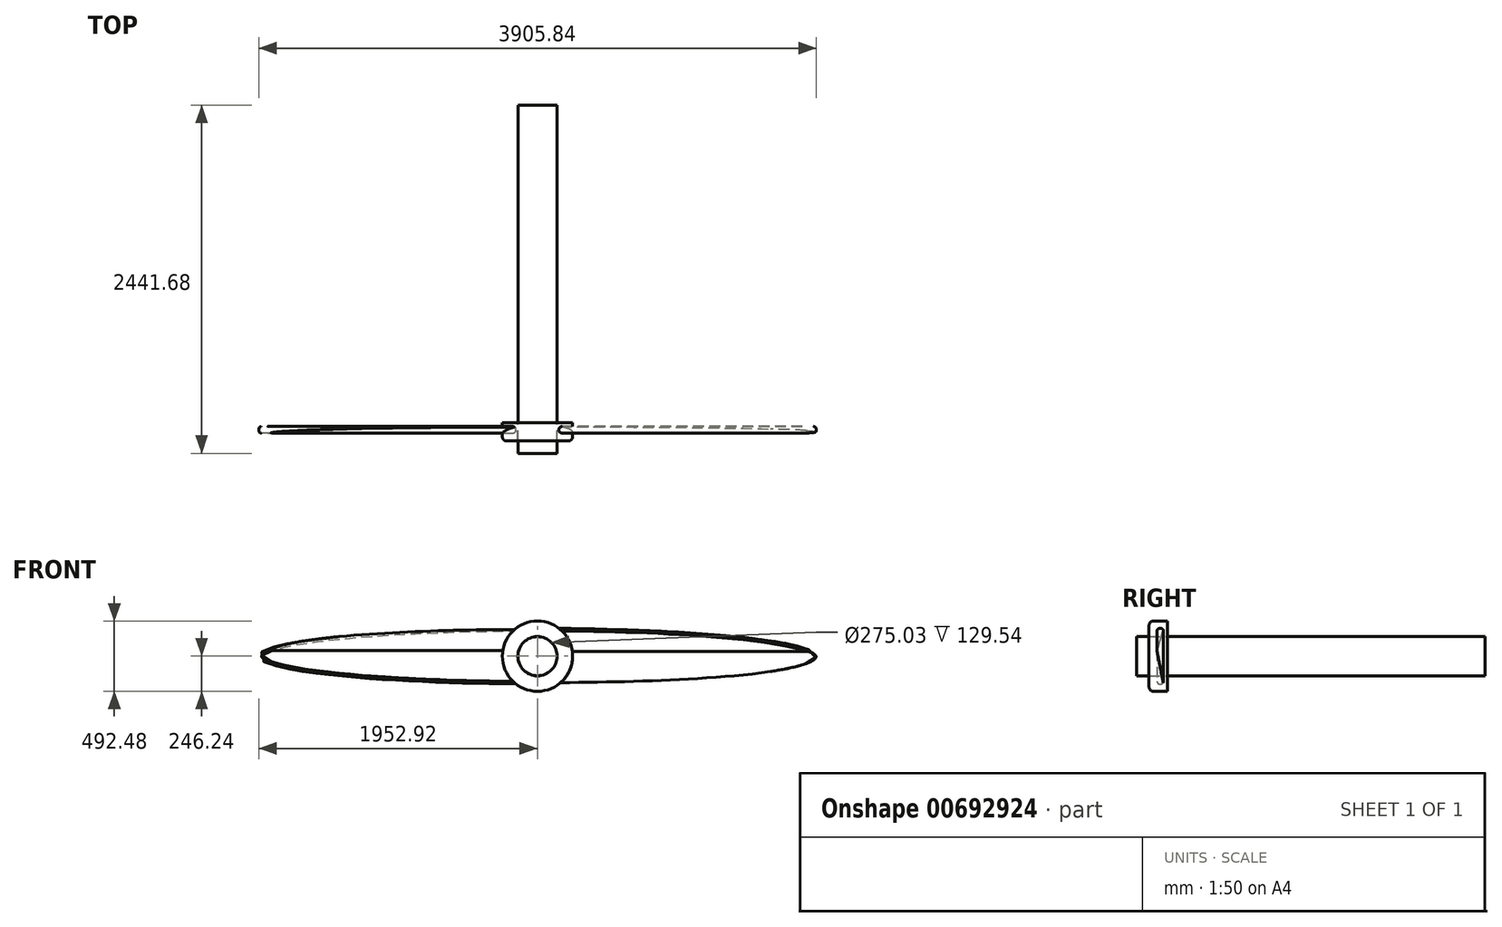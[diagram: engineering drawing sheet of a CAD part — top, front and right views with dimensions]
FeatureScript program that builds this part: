
annotation { "Feature Type Name" : "Feature", "Feature Type Description" : "" }
export const myFeature = defineFeature(function(context is Context, id is Id, definition is map)
    precondition{}
    {
        {
            var Q0;
            Q0=qCreatedBy(makeId("Front.planeOp"),FACE);
            var sketch = newSketch(context, id + "F0", { "sketchPlane" : qUnion([Q0])});
            skEllipse(sketch, "E0", {"center": v(0, 0) * mm, "majorRadius": 1952.92 * mm, "minorRadius": 195.14 * mm, "majorAxis": v(-1, 0)});
            skSolve(sketch);
        }
        {
            var Q0;
            Q0 = qSketchRegion(id + "F0", true);
            extrude(context, id + "F1", {"entities" : qUnion([Q0]), "endBound" : BoundingType.SYMMETRIC, "depth" : 45.2 * mm, "offsetDistance" : 25.4 * mm});
        }
        {
            var Q0;
            Q0=qCreatedBy(makeId("Front.planeOp"),FACE);
            var sketch = newSketch(context, id + "F2", { "sketchPlane" : qUnion([Q0])});
            skCircle(sketch, "E1", {"center": v(0, 0) * mm, "radius": 246.24 * mm});
            skCircle(sketch, "E2", {"center": v(0, 0) * mm, "radius": 137.51 * mm});
            skSolve(sketch);
        }
        {
            var Q0;
            Q0 = qSketchRegion(id + "F2", true);
            extrude(context, id + "F3", {"entities" : qUnion([Q0]), "operationType" : NewBodyOperationType.ADD, "endBound" : BoundingType.SYMMETRIC, "depth" : 101.6 * mm, "offsetDistance" : 25.4 * mm});
        }
        {
            var Q0;
            Q0=makeQuery(id+"F3.boolean.opBoolean","SPLIT",FACE,{"disambiguationData":[TD([makeQuery(id+"F3.opExtrude","SWEPT_FACE",FACE,{"disambiguationData":[OSD([sQuery(id+"F2.wireOp",EDGE,"E2")])]})])],"derivedFrom":makeQuery(id+"F1.opExtrude","CAP_FACE",FACE,{"disambiguationData":[OSD([sQuery(id+"F0.wireOp",EDGE,"E0")])],"isStart":false})});
            extrude(context, id + "F4", {"entities" : qUnion([Q0]), "operationType" : NewBodyOperationType.REMOVE, "oppositeDirection" : true, "depth" : 271.78 * mm, "offsetDistance" : 25.4 * mm});
        }
        {
            var Q0;
            Q0=qCreatedBy(makeId("Right.planeOp"),FACE);
            var sketch = newSketch(context, id + "F5", { "sketchPlane" : qUnion([Q0])});
            skLineSegment(sketch, "E3", {"start": v(21.4, 195.18) * mm, "end": v(-23.1, 39.15) * mm});
            skLineSegment(sketch, "E4", {"start": v(-23.1, 39.15) * mm, "end": v(-36.61, 208.7) * mm});
            skLineSegment(sketch, "E5", {"start": v(-36.61, 208.7) * mm, "end": v(21.4, 195.18) * mm});
            skSolve(sketch);
        }
        {
            var Q0;
            Q0 = qSketchRegion(id + "F5", true);
            extrude(context, id + "F6", {"entities" : qUnion([Q0]), "operationType" : NewBodyOperationType.REMOVE, "oppositeDirection" : true, "depth" : 2039.62 * mm, "offsetDistance" : 25.4 * mm});
        }
        {
            var Q0;
            Q0=makeQuery(id+"F3.boolean.opBoolean","SPLIT",EDGE,{"disambiguationData":[OD(0.0)],"derivedFrom":makeQuery(id+"F1.opExtrude","CAP_EDGE",EDGE,{"disambiguationData":[OSD([sQuery(id+"F0.wireOp",EDGE,"E0")])],"isStart":false})});
            var Q1;
            Q1=makeQuery(id+"F3.boolean.opBoolean","SPLIT",EDGE,{"disambiguationData":[OD(0.0)],"derivedFrom":makeQuery(id+"F1.opExtrude","CAP_EDGE",EDGE,{"disambiguationData":[OSD([sQuery(id+"F0.wireOp",EDGE,"E0")])],"isStart":true})});
            fillet(context, id + "F7", {"entities" : qUnion([Q0, Q1]), "radius" : 17.78 * mm, "tangentPropagation" : true, "allowEdgeOverflow" : false});
        }
        {
            var Q0;
            Q0=qCreatedBy(makeId("Right.planeOp"),FACE);
            var sketch = newSketch(context, id + "F8", { "sketchPlane" : qUnion([Q0])});
            skLineSegment(sketch, "E6", {"start": v(-23.02, 35.78) * mm, "end": v(28.56, -223.4) * mm});
            skLineSegment(sketch, "E7", {"start": v(28.56, -223.4) * mm, "end": v(-107.08, -223.4) * mm});
            skLineSegment(sketch, "E8", {"start": v(-107.08, -223.4) * mm, "end": v(-23.02, 35.78) * mm});
            skSolve(sketch);
        }
        {
            var Q0;
            Q0 = qSketchRegion(id + "F8", true);
            extrude(context, id + "F9", {"entities" : qUnion([Q0]), "operationType" : NewBodyOperationType.REMOVE, "depth" : 2032 * mm, "offsetDistance" : 25.4 * mm});
        }
        {
            var Q0;
            Q0=makeQuery(id+"F3.boolean.opBoolean","SPLIT",EDGE,{"disambiguationData":[OD(1.0)],"derivedFrom":makeQuery(id+"F1.opExtrude","CAP_EDGE",EDGE,{"disambiguationData":[OSD([sQuery(id+"F0.wireOp",EDGE,"E0")])],"isStart":false})});
            var Q1;
            Q1=makeQuery(id+"F3.boolean.opBoolean","SPLIT",EDGE,{"disambiguationData":[OD(1.0)],"derivedFrom":makeQuery(id+"F1.opExtrude","CAP_EDGE",EDGE,{"disambiguationData":[OSD([sQuery(id+"F0.wireOp",EDGE,"E0")])],"isStart":true})});
            fillet(context, id + "F10", {"entities" : qUnion([Q0, Q1]), "radius" : 17.17 * mm, "tangentPropagation" : true, "allowEdgeOverflow" : false});
        }
        {
            var Q0;
            Q0=makeQuery(id+"F3.opExtrude","CAP_FACE",FACE,{"disambiguationData":[OSD([sQuery(id+"F2.wireOp",EDGE,"E1"),sQuery(id+"F2.wireOp",EDGE,"E2")])],"isStart":true});
            extrude(context, id + "F11", {"entities" : qUnion([Q0]), "operationType" : NewBodyOperationType.ADD, "oppositeDirection" : true, "depth" : 129.54 * mm, "offsetDistance" : 25.4 * mm});
        }
        {
            var Q0;
            Q0=makeQuery(id+"F11.opExtrude","CAP_EDGE",EDGE,{"disambiguationData":[OSD([sQuery(id+"F2.wireOp",EDGE,"E1")])],"isStart":false});
            fillet(context, id + "F12", {"entities" : qUnion([Q0]), "radius" : 30.66 * mm, "tangentPropagation" : true, "allowEdgeOverflow" : false});
        }
        {
            var Q0;
            Q0=qCreatedBy(makeId("Front.planeOp"),FACE);
            var sketch = newSketch(context, id + "F13", { "sketchPlane" : qUnion([Q0])});
            skCircle(sketch, "E9", {"center": v(0, 0) * mm, "radius": 137.02 * mm});
            skSolve(sketch);
        }
        {
            var Q0;
            Q0=makeQuery(id+"F13.imprint","IMPRINT",FACE,{"disambiguationData":[TD([[makeQuery(id+"F13.imprint","IMPRINT",EDGE,{"derivedFrom":sQuery(id+"F13.wireOp",EDGE,"E9")}),1.0]])]});
            extrude(context, id + "F14", {"entities" : qUnion([Q0]), "endBound" : BoundingType.SYMMETRIC, "depth" : 331.74 * mm, "offsetDistance" : 25.4 * mm});
        }
        {
            var Q0;
            Q0=makeQuery(id+"F14.opExtrude","CAP_FACE",FACE,{"disambiguationData":[OSD([sQuery(id+"F13.wireOp",EDGE,"E9")])],"isStart":true});
            extrude(context, id + "F15", {"entities" : qUnion([Q0]), "operationType" : NewBodyOperationType.ADD, "depth" : 2109.94 * mm, "offsetDistance" : 25.4 * mm});
        }
    });
